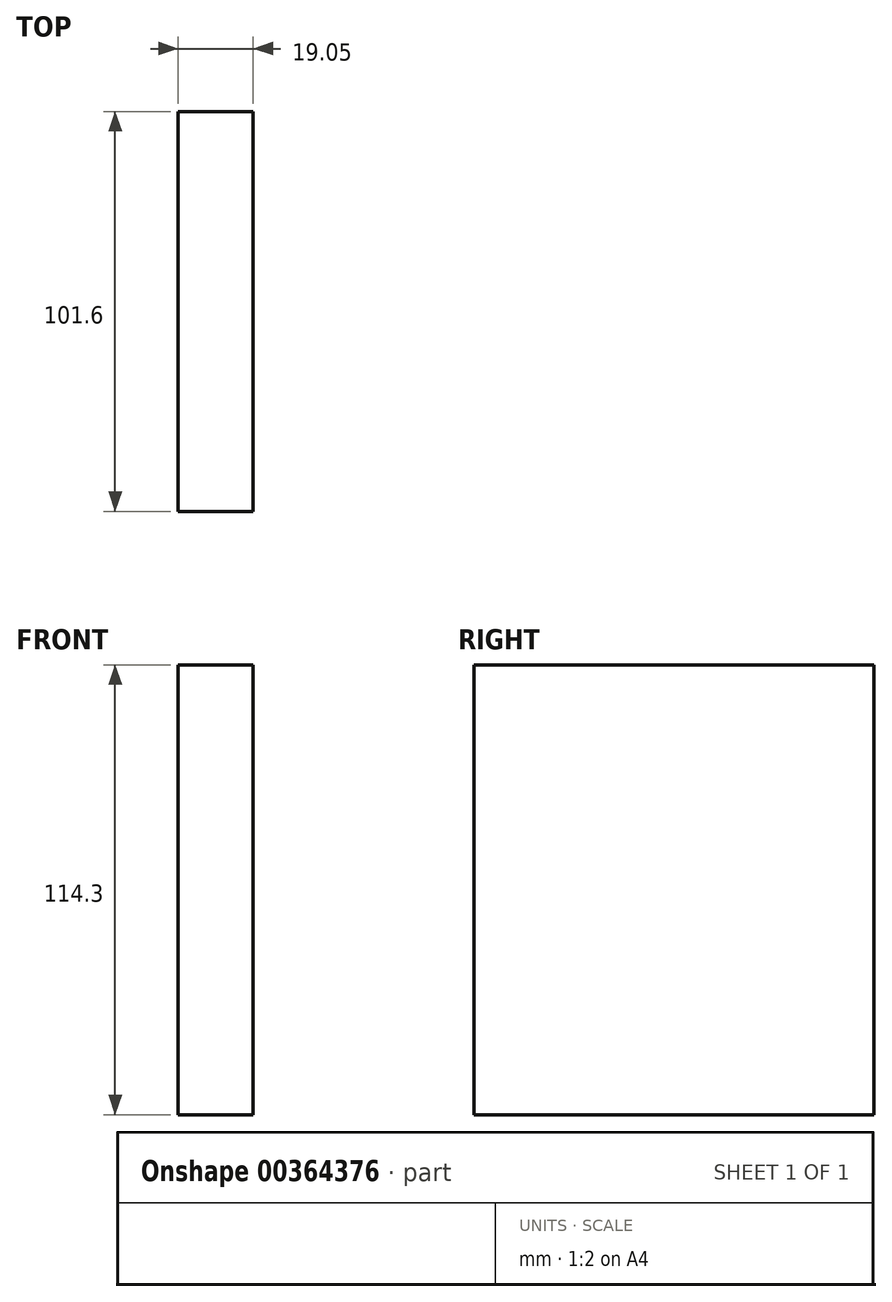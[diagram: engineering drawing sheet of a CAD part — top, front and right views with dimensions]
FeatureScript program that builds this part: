
annotation { "Feature Type Name" : "Feature", "Feature Type Description" : "" }
export const myFeature = defineFeature(function(context is Context, id is Id, definition is map)
    precondition{}
    {
        {
            var Q0;
            Q0=qCreatedBy(makeId("Right.planeOp"),FACE);
            var sketch = newSketch(context, id + "F0", { "sketchPlane" : qUnion([Q0])});
            skLineSegment(sketch, "E0.bottom", {"start": v(-79.8, 81.93) * mm, "end": v(21.8, 81.93) * mm});
            skLineSegment(sketch, "E0.top", {"start": v(-79.8, -32.37) * mm, "end": v(21.8, -32.37) * mm});
            skLineSegment(sketch, "E0.left", {"start": v(-79.8, 81.93) * mm, "end": v(-79.8, -32.37) * mm});
            skLineSegment(sketch, "E0.right", {"start": v(21.8, 81.93) * mm, "end": v(21.8, -32.37) * mm});
            skSolve(sketch);
        }
        {
            var Q0;
            Q0 = qSketchRegion(id + "F0", true);
            extrude(context, id + "F1", {"entities" : qUnion([Q0]), "depth" : 19.05 * mm});
        }
    });
